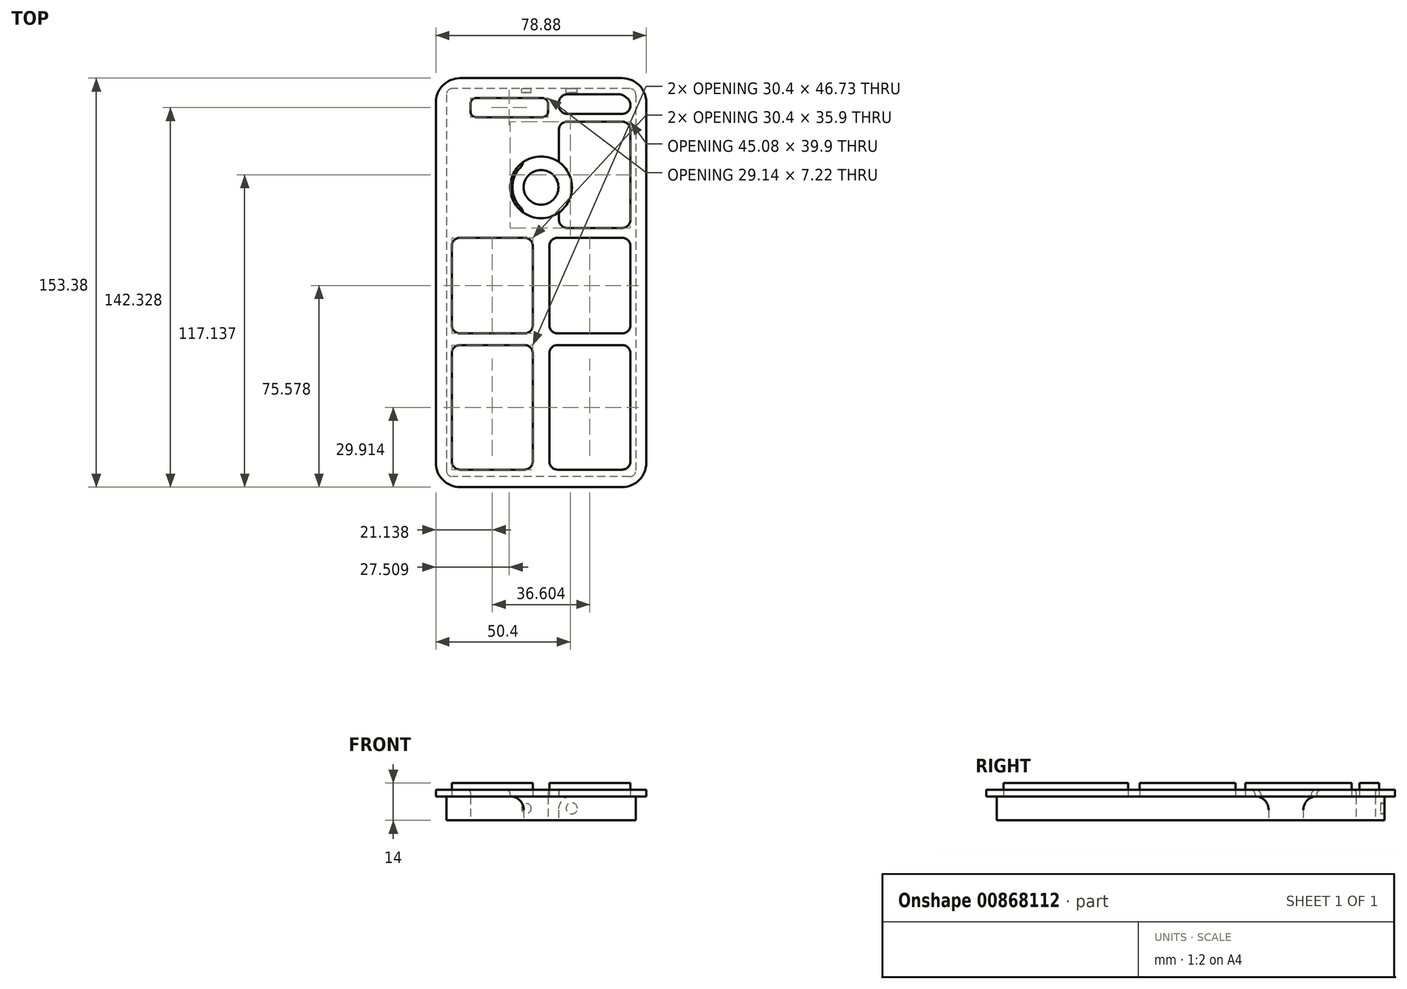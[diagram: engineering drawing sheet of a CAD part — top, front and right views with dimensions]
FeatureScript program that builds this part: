
annotation { "Feature Type Name" : "Feature", "Feature Type Description" : "" }
export const myFeature = defineFeature(function(context is Context, id is Id, definition is map)
    precondition{}
    {
        {
            var Q0;
            Q0=qCreatedBy(makeId("Top.planeOp"),FACE);
            var sketch = newSketch(context, id + "F0", { "sketchPlane" : qUnion([Q0])});
            skLineSegment(sketch, "E0.bottom", {"start": v(35.5, 72.75) * mm, "end": v(-35.5, 72.75) * mm});
            skLineSegment(sketch, "E0.top", {"start": v(35.5, -72.75) * mm, "end": v(-35.5, -72.75) * mm});
            skLineSegment(sketch, "E0.left", {"start": v(35.5, 72.75) * mm, "end": v(35.5, -72.75) * mm});
            skLineSegment(sketch, "E0.right", {"start": v(-35.5, 72.75) * mm, "end": v(-35.5, -72.75) * mm});
            skPoint(sketch, "E0.middle", {"position": v(0, 0) * mm});
            skCircle(sketch, "E1.MirrorC", {"center": v(0, 35.75) * mm, "radius": 6.5 * mm});
            skLineSegment(sketch, "E2.MirrorCS", {"start": v(-26.5, 62.03) * mm, "end": v(2.64, 62.03) * mm});
            skLineSegment(sketch, "E3.MirrorCS", {"start": v(-26.5, 69.25) * mm, "end": v(2.64, 69.25) * mm});
            skLineSegment(sketch, "E4.MirrorCS", {"start": v(-26.5, 69.25) * mm, "end": v(-26.5, 62.03) * mm});
            skLineSegment(sketch, "E5.MirrorCS", {"start": v(2.64, 69.25) * mm, "end": v(2.64, 62.03) * mm});
            skSolve(sketch);
        }
        {
            var Q0;
            Q0=makeQuery(id+"F0.imprint","IMPRINT",FACE,{"disambiguationData":[TD([[makeQuery(id+"F0.imprint","IMPRINT",EDGE,{"derivedFrom":sQuery(id+"F0.wireOp",EDGE,"E0.bottom")}),1.0]])]});
            extrude(context, id + "F1", {"entities" : qUnion([Q0]), "depth" : 9 * mm, "offsetDistance" : 25.4 * mm});
        }
        {
            var Q0;
            Q0=makeQuery(id+"F1.opExtrude","SWEPT_EDGE",EDGE,{"disambiguationData":[OSD([sQuery(id+"F0.wireOp",EDGE,"E3.MirrorCS"),sQuery(id+"F0.wireOp",EDGE,"E5.MirrorCS")])]});
            var Q1;
            Q1=makeQuery(id+"F1.opExtrude","SWEPT_EDGE",EDGE,{"disambiguationData":[OSD([sQuery(id+"F0.wireOp",EDGE,"E3.MirrorCS"),sQuery(id+"F0.wireOp",EDGE,"E4.MirrorCS")])]});
            var Q2;
            Q2=makeQuery(id+"F1.opExtrude","SWEPT_EDGE",EDGE,{"disambiguationData":[OSD([sQuery(id+"F0.wireOp",EDGE,"E2.MirrorCS"),sQuery(id+"F0.wireOp",EDGE,"E4.MirrorCS")])]});
            var Q3;
            Q3=makeQuery(id+"F1.opExtrude","SWEPT_EDGE",EDGE,{"disambiguationData":[OSD([sQuery(id+"F0.wireOp",EDGE,"E2.MirrorCS"),sQuery(id+"F0.wireOp",EDGE,"E5.MirrorCS")])]});
            var Q4;
            Q4=makeQuery(id+"F1.opExtrude","SWEPT_EDGE",EDGE,{"disambiguationData":[OSD([sQuery(id+"F0.wireOp",EDGE,"E0.top"),sQuery(id+"F0.wireOp",EDGE,"E0.right")])]});
            var Q5;
            Q5=makeQuery(id+"F1.opExtrude","SWEPT_EDGE",EDGE,{"disambiguationData":[OSD([sQuery(id+"F0.wireOp",EDGE,"E0.top"),sQuery(id+"F0.wireOp",EDGE,"E0.left")])]});
            var Q6;
            Q6=makeQuery(id+"F1.opExtrude","SWEPT_EDGE",EDGE,{"disambiguationData":[OSD([sQuery(id+"F0.wireOp",EDGE,"E0.bottom"),sQuery(id+"F0.wireOp",EDGE,"E0.left")])]});
            var Q7;
            Q7=makeQuery(id+"F1.opExtrude","SWEPT_EDGE",EDGE,{"disambiguationData":[OSD([sQuery(id+"F0.wireOp",EDGE,"E0.bottom"),sQuery(id+"F0.wireOp",EDGE,"E0.right")])]});
            fillet(context, id + "F2", {"entities" : qUnion([Q0, Q1, Q2, Q3, Q4, Q5, Q6, Q7]), "radius" : 2.2 * mm, "tangentPropagation" : true, "allowEdgeOverflow" : false});
        }
        {
            var Q0;
            Q0=makeQuery(id+"F1.opExtrude","CAP_EDGE",EDGE,{"disambiguationData":[OSD([sQuery(id+"F0.wireOp",EDGE,"E1.MirrorC")])],"isStart":false});
            fillet(context, id + "F3", {"entities" : qUnion([Q0]), "radius" : 5.08 * mm, "tangentPropagation" : true, "allowEdgeOverflow" : false});
        }
        {
            var Q0;
            Q0=makeQuery(id+"F1.opExtrude","CAP_FACE",FACE,{"disambiguationData":[OSD([sQuery(id+"F0.wireOp",EDGE,"E0.bottom"),sQuery(id+"F0.wireOp",EDGE,"E0.top"),sQuery(id+"F0.wireOp",EDGE,"E0.left"),sQuery(id+"F0.wireOp",EDGE,"E0.right"),sQuery(id+"F0.wireOp",EDGE,"E1.MirrorC"),sQuery(id+"F0.wireOp",EDGE,"E2.MirrorCS"),sQuery(id+"F0.wireOp",EDGE,"E3.MirrorCS"),sQuery(id+"F0.wireOp",EDGE,"E4.MirrorCS"),sQuery(id+"F0.wireOp",EDGE,"E5.MirrorCS")])],"isStart":false});
            var sketch = newSketch(context, id + "F4", { "sketchPlane" : qUnion([Q0])});
            skCircle(sketch, "E6", {"center": v(0, 35.75) * mm, "radius": 10.76 * mm});
            skLineSegment(sketch, "E7", {"start": v(-43.51, 44.15) * mm, "end": v(43.7, 44.15) * mm, "construction": true});
            skLineSegment(sketch, "E8", {"start": v(-6.72, 44.15) * mm, "end": v(-6.72, 60.4) * mm});
            skLineSegment(sketch, "E9", {"start": v(-6.72, 60.4) * mm, "end": v(-33.5, 60.4) * mm});
            skLineSegment(sketch, "E10", {"start": v(-33.5, 60.4) * mm, "end": v(-33.5, 20.5) * mm});
            skLineSegment(sketch, "E11", {"start": v(-33.5, 20.5) * mm, "end": v(-6.72, 20.5) * mm});
            skLineSegment(sketch, "E12", {"start": v(-6.72, 20.5) * mm, "end": v(-6.72, 27.35) * mm});
            skLineSegment(sketch, "E13.bottom", {"start": v(-33.5, 16.84) * mm, "end": v(-3.1, 16.84) * mm});
            skLineSegment(sketch, "E13.top", {"start": v(-33.5, -19.06) * mm, "end": v(-3.1, -19.06) * mm});
            skLineSegment(sketch, "E13.left", {"start": v(-33.5, 16.84) * mm, "end": v(-33.5, -19.06) * mm});
            skLineSegment(sketch, "E13.right", {"start": v(-3.1, 16.84) * mm, "end": v(-3.1, -19.06) * mm});
            skLineSegment(sketch, "E14.bottom", {"start": v(-33.5, -23.4) * mm, "end": v(-3.1, -23.4) * mm});
            skLineSegment(sketch, "E14.top", {"start": v(-33.5, -70.14) * mm, "end": v(-3.1, -70.14) * mm});
            skLineSegment(sketch, "E14.left", {"start": v(-33.5, -23.4) * mm, "end": v(-33.5, -70.14) * mm});
            skLineSegment(sketch, "E14.right", {"start": v(-3.1, -23.4) * mm, "end": v(-3.1, -70.14) * mm});
            skLineSegment(sketch, "E15", {"start": v(0, 84.68) * mm, "end": v(0, -85.43) * mm, "construction": true});
            skLineSegment(sketch, "E16.MirrorCS", {"start": v(6.72, 60.4) * mm, "end": v(33.5, 60.4) * mm});
            skLineSegment(sketch, "E17.MirrorCS", {"start": v(33.5, 60.4) * mm, "end": v(33.5, 20.5) * mm});
            skLineSegment(sketch, "E18.MirrorCS", {"start": v(6.72, 44.15) * mm, "end": v(6.72, 60.4) * mm});
            skLineSegment(sketch, "E19.MirrorCS", {"start": v(33.5, 20.5) * mm, "end": v(6.72, 20.5) * mm});
            skLineSegment(sketch, "E20.MirrorCS", {"start": v(6.72, 20.5) * mm, "end": v(6.72, 27.35) * mm});
            skLineSegment(sketch, "E21.MirrorCS", {"start": v(33.5, -19.06) * mm, "end": v(3.1, -19.06) * mm});
            skLineSegment(sketch, "E22.MirrorCS", {"start": v(33.5, 16.84) * mm, "end": v(33.5, -19.06) * mm});
            skLineSegment(sketch, "E23.MirrorCS", {"start": v(33.5, 16.84) * mm, "end": v(3.1, 16.84) * mm});
            skLineSegment(sketch, "E24.MirrorCS", {"start": v(3.1, 16.84) * mm, "end": v(3.1, -19.06) * mm});
            skLineSegment(sketch, "E25.MirrorCS", {"start": v(33.5, -23.4) * mm, "end": v(3.1, -23.4) * mm});
            skLineSegment(sketch, "E26.MirrorCS", {"start": v(33.5, -23.4) * mm, "end": v(33.5, -70.14) * mm});
            skLineSegment(sketch, "E27.MirrorCS", {"start": v(33.5, -70.14) * mm, "end": v(3.1, -70.14) * mm});
            skLineSegment(sketch, "E28.MirrorCS", {"start": v(3.1, -23.4) * mm, "end": v(3.1, -70.14) * mm});
            skLineSegment(sketch, "E29.bottom", {"start": v(6.72, 63.3) * mm, "end": v(33.5, 63.3) * mm});
            skLineSegment(sketch, "E29.left", {"start": v(6.72, 63.3) * mm, "end": v(6.72, 68.24) * mm});
            skLineSegment(sketch, "E29.right", {"start": v(33.5, 63.3) * mm, "end": v(33.5, 68.24) * mm});
            skLineSegment(sketch, "E30", {"start": v(6.72, 68.24) * mm, "end": v(6.72, 70.61) * mm});
            skLineSegment(sketch, "E31", {"start": v(6.72, 70.61) * mm, "end": v(30.42, 70.61) * mm});
            skLineSegment(sketch, "E32", {"start": v(30.42, 70.61) * mm, "end": v(33.5, 68.24) * mm});
            skSolve(sketch);
        }
        {
            var Q0;
            Q0=makeQuery(id+"F4.imprint","IMPRINT",FACE,{"disambiguationData":[TD([[makeQuery(id+"F4.imprint","IMPRINT",EDGE,{"derivedFrom":sQuery(id+"F4.wireOp",EDGE,"E13.bottom")}),-1.0]])]});
            var Q1;
            Q1=makeQuery(id+"F4.imprint","IMPRINT",FACE,{"disambiguationData":[TD([[makeQuery(id+"F4.imprint","IMPRINT",EDGE,{"derivedFrom":sQuery(id+"F4.wireOp",EDGE,"E14.bottom")}),-1.0]])]});
            var Q2;
            Q2=makeQuery(id+"F4.imprint","IMPRINT",FACE,{"disambiguationData":[TD([[makeQuery(id+"F4.imprint","IMPRINT",EDGE,{"derivedFrom":sQuery(id+"F4.wireOp",EDGE,"E21.MirrorCS")}),-1.0]])]});
            var Q3;
            Q3=makeQuery(id+"F4.imprint","IMPRINT",FACE,{"disambiguationData":[TD([[makeQuery(id+"F4.imprint","IMPRINT",EDGE,{"derivedFrom":sQuery(id+"F4.wireOp",EDGE,"E25.MirrorCS")}),1.0]])]});
            var Q4;
            Q4=makeQuery(id+"F4.imprint","IMPRINT",FACE,{"disambiguationData":[TD([[makeQuery(id+"F4.imprint","IMPRINT",EDGE,{"derivedFrom":sQuery(id+"F4.wireOp",EDGE,"E29.bottom")}),1.0]])]});
            var Q5;
            Q5=makeQuery(id+"F4.imprint","IMPRINT",FACE,{"disambiguationData":[TD([[makeQuery(id+"F4.imprint","IMPRINT",EDGE,{"derivedFrom":sQuery(id+"F4.wireOp",EDGE,"E16.MirrorCS")}),-1.0]])]});
            var Q6;
            {var subQ0=sQuery(id+"F4.wireOp",EDGE,"E8");Q6=makeQuery(id+"F4.imprint","IMPRINT",FACE,{"disambiguationData":[TD([[makeQuery(id+"F4.imprint","IMPRINT",EDGE,{"derivedFrom":subQ0}),1.0]])]});}
            extrude(context, id + "F5", {"entities" : qUnion([Q0, Q1, Q2, Q3, Q4, Q5, Q6]), "operationType" : NewBodyOperationType.ADD, "depth" : 5 * mm, "offsetDistance" : 25.4 * mm});
        }
        {
            var Q0;
            Q0=makeQuery(id+"F5.opExtrude","SWEPT_EDGE",EDGE,{"disambiguationData":[OSD([sQuery(id+"F4.wireOp",EDGE,"E14.top"),sQuery(id+"F4.wireOp",EDGE,"E14.left")])]});
            var Q1;
            Q1=makeQuery(id+"F5.opExtrude","SWEPT_EDGE",EDGE,{"disambiguationData":[OSD([sQuery(id+"F4.wireOp",EDGE,"E14.top"),sQuery(id+"F4.wireOp",EDGE,"E14.right")])]});
            var Q2;
            Q2=makeQuery(id+"F5.opExtrude","SWEPT_EDGE",EDGE,{"disambiguationData":[OSD([sQuery(id+"F4.wireOp",EDGE,"E27.MirrorCS"),sQuery(id+"F4.wireOp",EDGE,"E28.MirrorCS")])]});
            var Q3;
            Q3=makeQuery(id+"F5.opExtrude","SWEPT_EDGE",EDGE,{"disambiguationData":[OSD([sQuery(id+"F4.wireOp",EDGE,"E26.MirrorCS"),sQuery(id+"F4.wireOp",EDGE,"E27.MirrorCS")])]});
            var Q4;
            Q4=makeQuery(id+"F5.opExtrude","SWEPT_EDGE",EDGE,{"disambiguationData":[OSD([sQuery(id+"F4.wireOp",EDGE,"E21.MirrorCS"),sQuery(id+"F4.wireOp",EDGE,"E22.MirrorCS")])]});
            var Q5;
            Q5=makeQuery(id+"F5.opExtrude","SWEPT_EDGE",EDGE,{"disambiguationData":[OSD([sQuery(id+"F4.wireOp",EDGE,"E21.MirrorCS"),sQuery(id+"F4.wireOp",EDGE,"E24.MirrorCS")])]});
            var Q6;
            Q6=makeQuery(id+"F5.opExtrude","SWEPT_EDGE",EDGE,{"disambiguationData":[OSD([sQuery(id+"F4.wireOp",EDGE,"E14.bottom"),sQuery(id+"F4.wireOp",EDGE,"E14.right")])]});
            var Q7;
            Q7=makeQuery(id+"F5.opExtrude","SWEPT_EDGE",EDGE,{"disambiguationData":[OSD([sQuery(id+"F4.wireOp",EDGE,"E13.top"),sQuery(id+"F4.wireOp",EDGE,"E13.right")])]});
            var Q8;
            Q8=makeQuery(id+"F5.opExtrude","SWEPT_EDGE",EDGE,{"disambiguationData":[OSD([sQuery(id+"F4.wireOp",EDGE,"E13.top"),sQuery(id+"F4.wireOp",EDGE,"E13.left")])]});
            var Q9;
            Q9=makeQuery(id+"F5.opExtrude","SWEPT_EDGE",EDGE,{"disambiguationData":[OSD([sQuery(id+"F4.wireOp",EDGE,"E25.MirrorCS"),sQuery(id+"F4.wireOp",EDGE,"E26.MirrorCS")])]});
            var Q10;
            Q10=makeQuery(id+"F5.opExtrude","SWEPT_EDGE",EDGE,{"disambiguationData":[OSD([sQuery(id+"F4.wireOp",EDGE,"E25.MirrorCS"),sQuery(id+"F4.wireOp",EDGE,"E28.MirrorCS")])]});
            var Q11;
            Q11=makeQuery(id+"F5.opExtrude","SWEPT_EDGE",EDGE,{"disambiguationData":[OSD([sQuery(id+"F4.wireOp",EDGE,"E14.bottom"),sQuery(id+"F4.wireOp",EDGE,"E14.left")])]});
            var Q12;
            Q12=makeQuery(id+"F5.opExtrude","SWEPT_EDGE",EDGE,{"disambiguationData":[OSD([sQuery(id+"F4.wireOp",EDGE,"E13.bottom"),sQuery(id+"F4.wireOp",EDGE,"E13.right")])]});
            var Q13;
            Q13=makeQuery(id+"F5.opExtrude","SWEPT_EDGE",EDGE,{"disambiguationData":[OSD([sQuery(id+"F4.wireOp",EDGE,"E13.bottom"),sQuery(id+"F4.wireOp",EDGE,"E13.left")])]});
            var Q14;
            Q14=makeQuery(id+"F5.opExtrude","SWEPT_EDGE",EDGE,{"disambiguationData":[OSD([sQuery(id+"F4.wireOp",EDGE,"E11"),sQuery(id+"F4.wireOp",EDGE,"E12")])]});
            var Q15;
            Q15=makeQuery(id+"F5.opExtrude","SWEPT_EDGE",EDGE,{"disambiguationData":[OSD([sQuery(id+"F4.wireOp",EDGE,"E17.MirrorCS"),sQuery(id+"F4.wireOp",EDGE,"E19.MirrorCS")])]});
            var Q16;
            Q16=makeQuery(id+"F5.opExtrude","SWEPT_EDGE",EDGE,{"disambiguationData":[OSD([sQuery(id+"F4.wireOp",EDGE,"E22.MirrorCS"),sQuery(id+"F4.wireOp",EDGE,"E23.MirrorCS")])]});
            var Q17;
            Q17=makeQuery(id+"F5.opExtrude","SWEPT_EDGE",EDGE,{"disambiguationData":[OSD([sQuery(id+"F4.wireOp",EDGE,"E23.MirrorCS"),sQuery(id+"F4.wireOp",EDGE,"E24.MirrorCS")])]});
            var Q18;
            Q18=makeQuery(id+"F5.opExtrude","SWEPT_EDGE",EDGE,{"disambiguationData":[OSD([sQuery(id+"F4.wireOp",EDGE,"E16.MirrorCS"),sQuery(id+"F4.wireOp",EDGE,"E17.MirrorCS")])]});
            var Q19;
            Q19=makeQuery(id+"F5.opExtrude","SWEPT_EDGE",EDGE,{"disambiguationData":[OSD([sQuery(id+"F4.wireOp",EDGE,"E16.MirrorCS"),sQuery(id+"F4.wireOp",EDGE,"E18.MirrorCS")])]});
            var Q20;
            Q20=makeQuery(id+"F5.opExtrude","SWEPT_EDGE",EDGE,{"disambiguationData":[OSD([sQuery(id+"F4.wireOp",EDGE,"E29.right"),sQuery(id+"F4.wireOp",EDGE,"E32")])]});
            var Q21;
            Q21=makeQuery(id+"F5.opExtrude","SWEPT_EDGE",EDGE,{"disambiguationData":[OSD([sQuery(id+"F4.wireOp",EDGE,"E29.bottom"),sQuery(id+"F4.wireOp",EDGE,"E29.right")])]});
            var Q22;
            Q22=makeQuery(id+"F5.opExtrude","SWEPT_EDGE",EDGE,{"disambiguationData":[OSD([sQuery(id+"F4.wireOp",EDGE,"E31"),sQuery(id+"F4.wireOp",EDGE,"E32")])]});
            var Q23;
            Q23=makeQuery(id+"F5.opExtrude","SWEPT_EDGE",EDGE,{"disambiguationData":[OSD([sQuery(id+"F4.wireOp",EDGE,"E30"),sQuery(id+"F4.wireOp",EDGE,"E31")])]});
            var Q24;
            Q24=makeQuery(id+"F5.opExtrude","SWEPT_EDGE",EDGE,{"disambiguationData":[OSD([sQuery(id+"F4.wireOp",EDGE,"E8"),sQuery(id+"F4.wireOp",EDGE,"E9")])]});
            var Q25;
            Q25=makeQuery(id+"F5.opExtrude","SWEPT_EDGE",EDGE,{"disambiguationData":[OSD([sQuery(id+"F4.wireOp",EDGE,"E29.bottom"),sQuery(id+"F4.wireOp",EDGE,"E29.left")])]});
            var Q26;
            Q26=makeQuery(id+"F5.opExtrude","SWEPT_EDGE",EDGE,{"disambiguationData":[OSD([sQuery(id+"F4.wireOp",EDGE,"E19.MirrorCS"),sQuery(id+"F4.wireOp",EDGE,"E20.MirrorCS")])]});
            var Q27;
            Q27=makeQuery(id+"F5.opExtrude","SWEPT_EDGE",EDGE,{"disambiguationData":[OSD([sQuery(id+"F4.wireOp",EDGE,"E10"),sQuery(id+"F4.wireOp",EDGE,"E11")])]});
            var Q28;
            Q28=makeQuery(id+"F5.opExtrude","SWEPT_EDGE",EDGE,{"disambiguationData":[OSD([sQuery(id+"F4.wireOp",EDGE,"E9"),sQuery(id+"F4.wireOp",EDGE,"E10")])]});
            fillet(context, id + "F6", {"entities" : qUnion([Q0, Q1, Q2, Q3, Q4, Q5, Q6, Q7, Q8, Q9, Q10, Q11, Q12, Q13, Q14, Q15, Q16, Q17, Q18, Q19, Q20, Q21, Q22, Q23, Q24, Q25, Q26, Q27, Q28]), "radius" : 3.07 * mm, "tangentPropagation" : true, "allowEdgeOverflow" : false});
        }
        {
            var Q0;
            Q0=makeQuery(id+"F1.opExtrude","CAP_FACE",FACE,{"disambiguationData":[OSD([sQuery(id+"F0.wireOp",EDGE,"E0.bottom"),sQuery(id+"F0.wireOp",EDGE,"E0.top"),sQuery(id+"F0.wireOp",EDGE,"E0.left"),sQuery(id+"F0.wireOp",EDGE,"E0.right"),sQuery(id+"F0.wireOp",EDGE,"E1.MirrorC"),sQuery(id+"F0.wireOp",EDGE,"E2.MirrorCS"),sQuery(id+"F0.wireOp",EDGE,"E3.MirrorCS"),sQuery(id+"F0.wireOp",EDGE,"E4.MirrorCS"),sQuery(id+"F0.wireOp",EDGE,"E5.MirrorCS")])],"isStart":false});
            var sketch = newSketch(context, id + "F7", { "sketchPlane" : qUnion([Q0])});
            skArc(sketch, "E33.0", {"start": v(-39.44, -67.67) * mm, "mid": v(-36.8, -74.05) * mm, "end": v(-30.42, -76.69) * mm});
            skLineSegment(sketch, "E33.1", {"start": v(-39.44, 67.67) * mm, "end": v(-39.44, -67.67) * mm});
            skLineSegment(sketch, "E33.2", {"start": v(-30.42, -76.69) * mm, "end": v(30.42, -76.69) * mm});
            skArc(sketch, "E33.3", {"start": v(-30.42, 76.69) * mm, "mid": v(-36.8, 74.05) * mm, "end": v(-39.44, 67.67) * mm});
            skArc(sketch, "E33.4", {"start": v(30.42, -76.69) * mm, "mid": v(36.8, -74.05) * mm, "end": v(39.44, -67.67) * mm});
            skLineSegment(sketch, "E33.5", {"start": v(39.44, -67.67) * mm, "end": v(39.44, 67.67) * mm});
            skArc(sketch, "E33.6", {"start": v(39.44, 67.67) * mm, "mid": v(36.8, 74.05) * mm, "end": v(30.42, 76.69) * mm});
            skLineSegment(sketch, "E33.7", {"start": v(30.42, 76.69) * mm, "end": v(-30.42, 76.69) * mm});
            skSolve(sketch);
        }
        {
            var Q0;
            Q0=makeQuery(id+"F7.imprint","IMPRINT",FACE,{"disambiguationData":[TD([[makeQuery(id+"F7.imprint","IMPRINT",EDGE,{"derivedFrom":sQuery(id+"F7.wireOp",EDGE,"E33.0")}),1.0]])]});
            var Q1;
            {var subQ8=sQuery(id+"F0.wireOp",EDGE,"E0.bottom");Q1=makeQuery(id+"F7.imprint","IMPRINT",FACE,{"disambiguationData":[TD([[makeQuery(id+"F7.imprint","IMPRINT",EDGE,{"derivedFrom":makeQuery(id+"F1.opExtrude","CAP_EDGE",EDGE,{"disambiguationData":[OSD([subQ8])],"isStart":false})}),1.0]])]});}
            extrude(context, id + "F8", {"entities" : qUnion([Q0, Q1]), "depth" : 2.5 * mm, "offsetDistance" : 25.4 * mm});
        }
        {
            var Q0;
            {var subQ0=sQuery(id+"F0.wireOp",EDGE,"E5.MirrorCS");var subQ1=sQuery(id+"F0.wireOp",EDGE,"E4.MirrorCS");var subQ2=sQuery(id+"F0.wireOp",EDGE,"E3.MirrorCS");var subQ3=sQuery(id+"F0.wireOp",EDGE,"E2.MirrorCS");var subQ4=sQuery(id+"F0.wireOp",EDGE,"E1.MirrorC");var subQ5=sQuery(id+"F0.wireOp",EDGE,"E0.right");var subQ6=sQuery(id+"F0.wireOp",EDGE,"E0.left");var subQ7=sQuery(id+"F0.wireOp",EDGE,"E0.top");var subQ8=sQuery(id+"F0.wireOp",EDGE,"E0.bottom");Q0=makeQuery(id+"F8.opExtrude","CAP_EDGE",EDGE,{"disambiguationData":[OSD([subQ8,subQ7,subQ6,subQ5,subQ4,subQ3,subQ2,subQ1,subQ0]),TDD([makeQuery(id+"F7.imprint","IMPRINT",EDGE,{"derivedFrom":makeQuery(id+"F2.opFillet","BLEND_EDGE",EDGE,{"blendedFrom":[makeQuery(id+"F1.opExtrude","SWEPT_EDGE",EDGE,{"disambiguationData":[OSD([subQ3,subQ0])]}),makeQuery(id+"F1.opExtrude","CAP_FACE",FACE,{"disambiguationData":[OSD([subQ8,subQ7,subQ6,subQ5,subQ4,subQ3,subQ2,subQ1,subQ0])],"isStart":false})],"blendedInto":[makeQuery(id+"F1.opExtrude","CAP_FACE",FACE,{"disambiguationData":[OSD([subQ8,subQ7,subQ6,subQ5,subQ4,subQ3,subQ2,subQ1,subQ0])],"isStart":false})]})})])],"isStart":false});}
            var Q1;
            Q1=makeQuery(id+"F8.opExtrude","CAP_EDGE",EDGE,{"disambiguationData":[OSD([sQuery(id+"F0.wireOp",EDGE,"E5.MirrorCS")])],"isStart":false});
            var Q2;
            {var subQ0=sQuery(id+"F0.wireOp",EDGE,"E5.MirrorCS");var subQ1=sQuery(id+"F0.wireOp",EDGE,"E4.MirrorCS");var subQ2=sQuery(id+"F0.wireOp",EDGE,"E3.MirrorCS");var subQ3=sQuery(id+"F0.wireOp",EDGE,"E2.MirrorCS");var subQ4=sQuery(id+"F0.wireOp",EDGE,"E1.MirrorC");var subQ5=sQuery(id+"F0.wireOp",EDGE,"E0.right");var subQ6=sQuery(id+"F0.wireOp",EDGE,"E0.left");var subQ7=sQuery(id+"F0.wireOp",EDGE,"E0.top");var subQ8=sQuery(id+"F0.wireOp",EDGE,"E0.bottom");Q2=makeQuery(id+"F8.opExtrude","CAP_EDGE",EDGE,{"disambiguationData":[OSD([subQ8,subQ7,subQ6,subQ5,subQ4,subQ3,subQ2,subQ1,subQ0]),TDD([makeQuery(id+"F7.imprint","IMPRINT",EDGE,{"derivedFrom":makeQuery(id+"F2.opFillet","BLEND_EDGE",EDGE,{"blendedFrom":[makeQuery(id+"F1.opExtrude","SWEPT_EDGE",EDGE,{"disambiguationData":[OSD([subQ2,subQ0])]}),makeQuery(id+"F1.opExtrude","CAP_FACE",FACE,{"disambiguationData":[OSD([subQ8,subQ7,subQ6,subQ5,subQ4,subQ3,subQ2,subQ1,subQ0])],"isStart":false})],"blendedInto":[makeQuery(id+"F1.opExtrude","CAP_FACE",FACE,{"disambiguationData":[OSD([subQ8,subQ7,subQ6,subQ5,subQ4,subQ3,subQ2,subQ1,subQ0])],"isStart":false})]})})])],"isStart":false});}
            var Q3;
            Q3=makeQuery(id+"F8.opExtrude","CAP_EDGE",EDGE,{"disambiguationData":[OSD([sQuery(id+"F0.wireOp",EDGE,"E3.MirrorCS")])],"isStart":false});
            var Q4;
            Q4=makeQuery(id+"F8.opExtrude","CAP_EDGE",EDGE,{"disambiguationData":[OSD([sQuery(id+"F0.wireOp",EDGE,"E2.MirrorCS")])],"isStart":false});
            var Q5;
            {var subQ0=sQuery(id+"F0.wireOp",EDGE,"E5.MirrorCS");var subQ1=sQuery(id+"F0.wireOp",EDGE,"E4.MirrorCS");var subQ2=sQuery(id+"F0.wireOp",EDGE,"E3.MirrorCS");var subQ3=sQuery(id+"F0.wireOp",EDGE,"E2.MirrorCS");var subQ4=sQuery(id+"F0.wireOp",EDGE,"E1.MirrorC");var subQ5=sQuery(id+"F0.wireOp",EDGE,"E0.right");var subQ6=sQuery(id+"F0.wireOp",EDGE,"E0.left");var subQ7=sQuery(id+"F0.wireOp",EDGE,"E0.top");var subQ8=sQuery(id+"F0.wireOp",EDGE,"E0.bottom");Q5=makeQuery(id+"F8.opExtrude","CAP_EDGE",EDGE,{"disambiguationData":[OSD([subQ8,subQ7,subQ6,subQ5,subQ4,subQ3,subQ2,subQ1,subQ0]),TDD([makeQuery(id+"F7.imprint","IMPRINT",EDGE,{"derivedFrom":makeQuery(id+"F2.opFillet","BLEND_EDGE",EDGE,{"blendedFrom":[makeQuery(id+"F1.opExtrude","SWEPT_EDGE",EDGE,{"disambiguationData":[OSD([subQ2,subQ1])]}),makeQuery(id+"F1.opExtrude","CAP_FACE",FACE,{"disambiguationData":[OSD([subQ8,subQ7,subQ6,subQ5,subQ4,subQ3,subQ2,subQ1,subQ0])],"isStart":false})],"blendedInto":[makeQuery(id+"F1.opExtrude","CAP_FACE",FACE,{"disambiguationData":[OSD([subQ8,subQ7,subQ6,subQ5,subQ4,subQ3,subQ2,subQ1,subQ0])],"isStart":false})]})})])],"isStart":false});}
            var Q6;
            Q6=makeQuery(id+"F8.opExtrude","CAP_EDGE",EDGE,{"disambiguationData":[OSD([sQuery(id+"F0.wireOp",EDGE,"E4.MirrorCS")])],"isStart":false});
            var Q7;
            {var subQ0=sQuery(id+"F0.wireOp",EDGE,"E5.MirrorCS");var subQ1=sQuery(id+"F0.wireOp",EDGE,"E4.MirrorCS");var subQ2=sQuery(id+"F0.wireOp",EDGE,"E3.MirrorCS");var subQ3=sQuery(id+"F0.wireOp",EDGE,"E2.MirrorCS");var subQ4=sQuery(id+"F0.wireOp",EDGE,"E1.MirrorC");var subQ5=sQuery(id+"F0.wireOp",EDGE,"E0.right");var subQ6=sQuery(id+"F0.wireOp",EDGE,"E0.left");var subQ7=sQuery(id+"F0.wireOp",EDGE,"E0.top");var subQ8=sQuery(id+"F0.wireOp",EDGE,"E0.bottom");Q7=makeQuery(id+"F8.opExtrude","CAP_EDGE",EDGE,{"disambiguationData":[OSD([subQ8,subQ7,subQ6,subQ5,subQ4,subQ3,subQ2,subQ1,subQ0]),TDD([makeQuery(id+"F7.imprint","IMPRINT",EDGE,{"derivedFrom":makeQuery(id+"F2.opFillet","BLEND_EDGE",EDGE,{"blendedFrom":[makeQuery(id+"F1.opExtrude","SWEPT_EDGE",EDGE,{"disambiguationData":[OSD([subQ3,subQ1])]}),makeQuery(id+"F1.opExtrude","CAP_FACE",FACE,{"disambiguationData":[OSD([subQ8,subQ7,subQ6,subQ5,subQ4,subQ3,subQ2,subQ1,subQ0])],"isStart":false})],"blendedInto":[makeQuery(id+"F1.opExtrude","CAP_FACE",FACE,{"disambiguationData":[OSD([subQ8,subQ7,subQ6,subQ5,subQ4,subQ3,subQ2,subQ1,subQ0])],"isStart":false})]})})])],"isStart":false});}
            fillet(context, id + "F9", {"entities" : qUnion([Q0, Q1, Q2, Q3, Q4, Q5, Q6, Q7]), "radius" : 1.17 * mm, "tangentPropagation" : true, "allowEdgeOverflow" : false});
        }
        {
            var Q0;
            {var subQ0=sQuery(id+"F0.wireOp",EDGE,"E5.MirrorCS");var subQ1=sQuery(id+"F0.wireOp",EDGE,"E4.MirrorCS");var subQ2=sQuery(id+"F0.wireOp",EDGE,"E3.MirrorCS");var subQ3=sQuery(id+"F0.wireOp",EDGE,"E2.MirrorCS");var subQ4=sQuery(id+"F0.wireOp",EDGE,"E1.MirrorC");var subQ5=sQuery(id+"F0.wireOp",EDGE,"E0.right");var subQ6=sQuery(id+"F0.wireOp",EDGE,"E0.left");var subQ7=sQuery(id+"F0.wireOp",EDGE,"E0.top");var subQ8=sQuery(id+"F0.wireOp",EDGE,"E0.bottom");Q0=makeQuery(id+"F8.opExtrude","CAP_EDGE",EDGE,{"disambiguationData":[OSD([subQ8,subQ7,subQ6,subQ5,subQ4,subQ3,subQ2,subQ1,subQ0]),TDD([makeQuery(id+"F7.imprint","IMPRINT",EDGE,{"derivedFrom":makeQuery(id+"F3.opFillet","BLEND_EDGE",EDGE,{"blendedFrom":[makeQuery(id+"F1.opExtrude","CAP_EDGE",EDGE,{"disambiguationData":[OSD([subQ4])],"isStart":false}),makeQuery(id+"F1.opExtrude","CAP_FACE",FACE,{"disambiguationData":[OSD([subQ8,subQ7,subQ6,subQ5,subQ4,subQ3,subQ2,subQ1,subQ0])],"isStart":false})],"blendedInto":[makeQuery(id+"F1.opExtrude","CAP_FACE",FACE,{"disambiguationData":[OSD([subQ8,subQ7,subQ6,subQ5,subQ4,subQ3,subQ2,subQ1,subQ0])],"isStart":false})]})})])],"isStart":false});}
            fillet(context, id + "F10", {"entities" : qUnion([Q0]), "radius" : 1.84 * mm, "tangentPropagation" : true, "allowEdgeOverflow" : false});
        }
        {
            var Q0;
            Q0=makeQuery(id+"F1.opExtrude","SWEPT_FACE",FACE,{"disambiguationData":[OSD([sQuery(id+"F0.wireOp",EDGE,"E0.bottom")])]});
            var sketch = newSketch(context, id + "F11", { "sketchPlane" : qUnion([Q0])});
            skLineSegment(sketch, "E34", {"start": v(-35.5, 4.5) * mm, "end": v(-11.5, 4.5) * mm, "construction": true});
            skLineSegment(sketch, "E35", {"start": v(35.5, 4.5) * mm, "end": v(5.5, 4.5) * mm, "construction": true});
            skCircle(sketch, "E36", {"center": v(5.5, 4.5) * mm, "radius": 1.83 * mm});
            skCircle(sketch, "E37", {"center": v(-11.5, 4.5) * mm, "radius": 2.1 * mm});
            skSolve(sketch);
        }
        {
            var Q0;
            Q0 = qSketchRegion(id + "F11", true);
            extrude(context, id + "F12", {"entities" : qUnion([Q0]), "operationType" : NewBodyOperationType.REMOVE, "oppositeDirection" : true, "depth" : 1.52 * mm, "offsetDistance" : 25.4 * mm});
        }
    });
